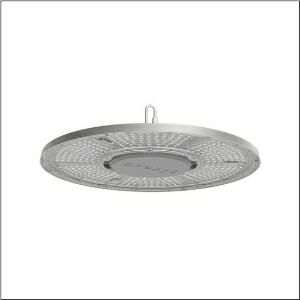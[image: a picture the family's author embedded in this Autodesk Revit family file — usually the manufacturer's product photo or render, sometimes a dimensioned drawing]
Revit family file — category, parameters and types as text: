
# Revit family: highbay_31-l_51hc42da4jmb
name_source: partatom
category: Lighting Fixtures
units: mm (PartAtom-declared; Revit-internal decimal feet)

## family parameters
Cut with Voids When Loaded = No
Host = Face
Light Source = No
Part Type = Normal
Room Calculation Point = No
Round Connector Dimension = Use Diameter
Shared = No

## types (1)
- Highbay 31-L (1 x LED, 20000 lm, 134 W, 4000K)
    Apparent Load = 134 VA
    CIE Flux Codes = 77 99 100 100 100
    Color Rendering = 80
    Color Temperature = 4000K
    Default Elevation = 1800 mm
    Description = Highbay 31-L, high bay luminaire, primary light control with lens, of PC, primary optical cover: cover panel, of PC, transparent, light emission: direct distribution, primary light characteristic: rotationally symmetric, installation type: suspended mounting, surface-mounted, LED, rated luminous flux: 20.000lm, luminous efficacy: 150lm/W, light colour: 840, colour temperature: 4000K, control gear: DALI 2, with cable, 5x 1.0mm², free wire ends, mains connection: 220..240V, AC/DC, 0/50..60Hz, cable length: 1,5m, rated input power: 134W, housing, rotationally symmetric, of diecast aluminium, powder-coated, grey aluminium (RAL 9007), with hook on luminaire side, incl. screw, diameter: 404mm, protection rating (complete): IP65, insulation class (complete): insulation class I (protective earthing), certification: CE, ENEC, UKCA, protection symbol: D, impact resistance: IK08, permissible operating ambient temperature: -30..+45°C, standard: EN 60598-2-22, EN 60598, corresponds to IFS (International Featured Standards) requirements for safety and quality in the food industry, packaging unit: 1 piece
    Height = 141 mm
    Lamp = 1 x LED
    Lamp Light Flux = 20000 lm
    Lamp Power = 134 W
    Lamp count = 1
    Length = 406 mm
    Luminous efficacy = 149 lm/W
    Manufacturer = Siteco
    ModVariant = No
    Model = 51HC42DA4JMB
    Mounting Place = Ceiling
    Mounting Type = Pendant
    Number of Poles = 1
    OnlyDefault = Yes
    Power Factor = 1
    Product Name = Highbay 31-L
    Product group = high bay luminaire
    ProductGroupID = 901
    Protection Class = Protection class I
    Protection Degree = IP 65
    RLX_Detail_Level = 1
    RLX_Emergency_Light_Flux = 0 lm
    RLX_Emergency_Type = 0
    RLX_Emergency_Type_DB = No
    RlxData = <blob elided: 172613 chars, md5=cfa3795d>
    Socket = socket
    Standby Power = 0 W
    System Light Flux = 20000 lm
    System Power = 134 W
    Type Comments = Product without accessories
    Type Image = l_1003610.jpg
    URL = http://relux.com
    VarID = ---
    Voltage = 0 V
    Weight = 0.00 kg
    Width = 0 mm  [stored 0 ft]

note: [stored X ft] marks values corroborated as IEEE doubles in the binary element streams (Revit-internal decimal feet)

## geometry (parser evidence)
native form markers: Blend x4, Sweep x10
no freeform markers — native parametric forms only
